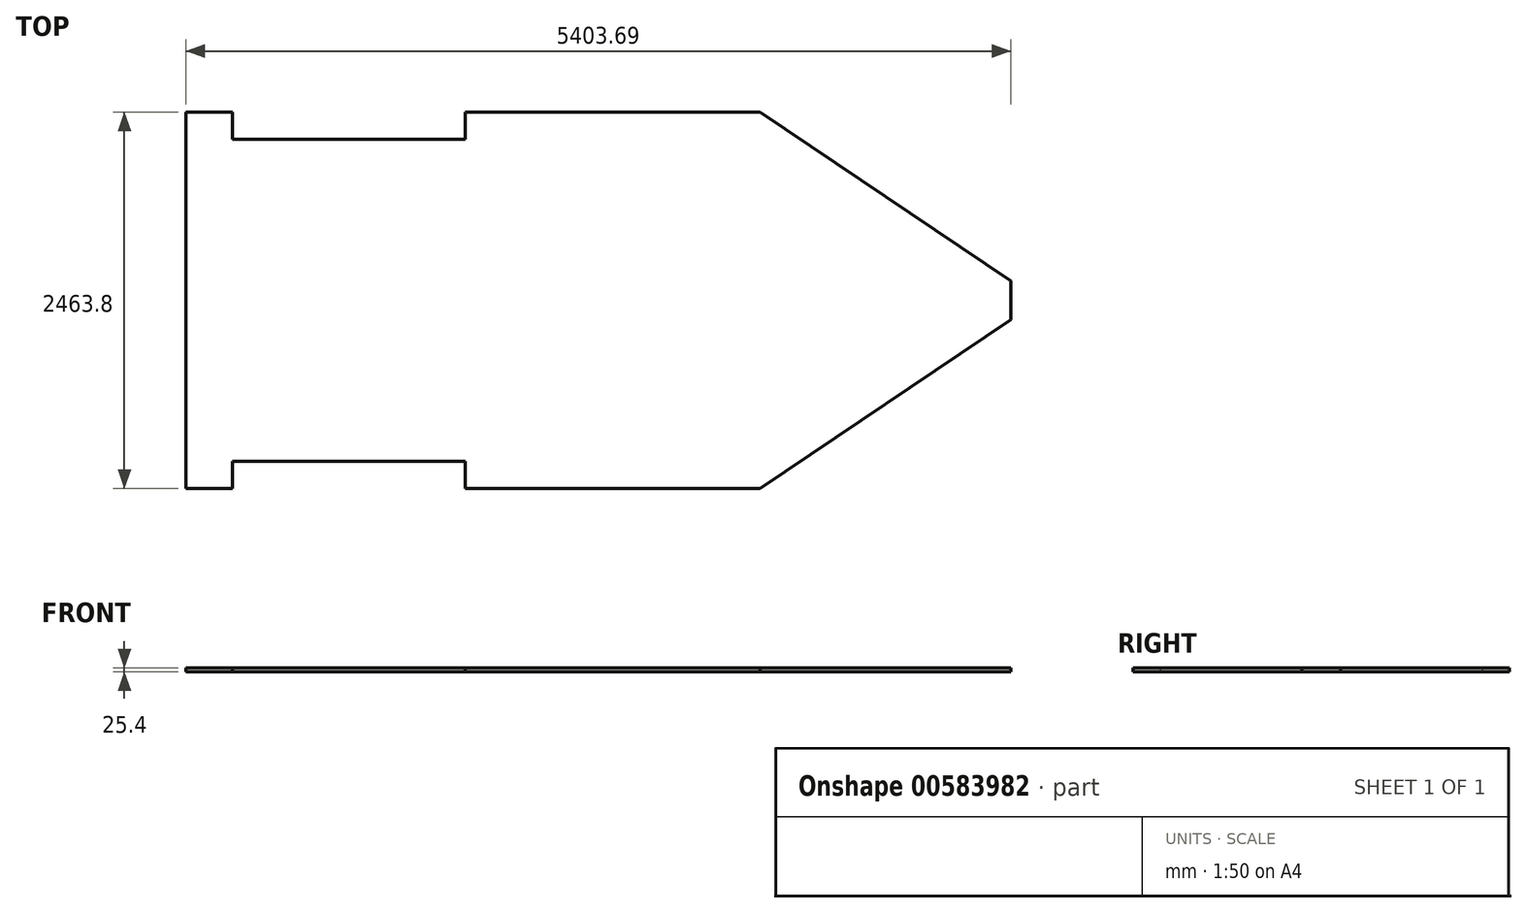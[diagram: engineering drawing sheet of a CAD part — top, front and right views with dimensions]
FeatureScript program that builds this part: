
annotation { "Feature Type Name" : "Feature", "Feature Type Description" : "" }
export const myFeature = defineFeature(function(context is Context, id is Id, definition is map)
    precondition{}
    {
        {
            var Q0;
            Q0=qCreatedBy(makeId("Top.planeOp"),FACE);
            var sketch = newSketch(context, id + "F0", { "sketchPlane" : qUnion([Q0])});
            skLineSegment(sketch, "E0", {"start": v(-390.5, 1002.4) * mm, "end": v(-390.5, 824.6) * mm});
            skLineSegment(sketch, "E1", {"start": v(-390.5, 824.6) * mm, "end": v(1133.5, 824.6) * mm});
            skLineSegment(sketch, "E2", {"start": v(1133.5, 824.6) * mm, "end": v(1133.5, 1002.4) * mm});
            skLineSegment(sketch, "E3", {"start": v(1133.5, 1002.4) * mm, "end": v(3063.9, 1002.4) * mm});
            skLineSegment(sketch, "E4", {"start": v(-390.5, -1283.6) * mm, "end": v(1133.5, -1283.6) * mm});
            skLineSegment(sketch, "E5", {"start": v(1133.5, -1283.6) * mm, "end": v(1133.5, -1461.4) * mm});
            skLineSegment(sketch, "E6", {"start": v(1133.5, -1461.4) * mm, "end": v(3063.9, -1461.4) * mm});
            skLineSegment(sketch, "E7", {"start": v(3063.9, 1002.4) * mm, "end": v(4708.4, -102.5) * mm});
            skLineSegment(sketch, "E8", {"start": v(4708.4, -102.5) * mm, "end": v(4708.4, -356.5) * mm});
            skLineSegment(sketch, "E9", {"start": v(4708.4, -356.5) * mm, "end": v(3063.9, -1461.4) * mm});
            skLineSegment(sketch, "E10.trimOffspring", {"start": v(-390.5, -1283.6) * mm, "end": v(-390.5, -1461.4) * mm});
            skLineSegment(sketch, "E11", {"start": v(-695.3, 1002.4) * mm, "end": v(-695.3, 1002.4) * mm});
            skLineSegment(sketch, "E12", {"start": v(-695.3, 1002.4) * mm, "end": v(-695.3, -1461.4) * mm});
            skLineSegment(sketch, "E13", {"start": v(-695.3, 1002.4) * mm, "end": v(-390.5, 1002.4) * mm});
            skLineSegment(sketch, "E14", {"start": v(-695.3, -1461.4) * mm, "end": v(-390.5, -1461.4) * mm});
            skSolve(sketch);
        }
        {
            var Q0;
            Q0=makeQuery(id+"F0.imprint","IMPRINT",FACE,{"disambiguationData":[TD([[makeQuery(id+"F0.imprint","IMPRINT",EDGE,{"derivedFrom":sQuery(id+"F0.wireOp",EDGE,"E0")}),-1.0]])]});
            extrude(context, id + "F1", {"entities" : qUnion([Q0]), "depth" : 25.4 * mm, "offsetDistance" : 25.4 * mm});
        }
    });
